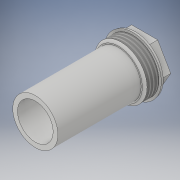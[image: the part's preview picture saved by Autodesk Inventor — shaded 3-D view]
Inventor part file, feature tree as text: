
AUTODESK INVENTOR PART (.ipt)
format: ipt  version: 2019 (Build 230136000, 136)  size: 149,504 bytes
history: native  units: mm
features: other x2, chamfer x2, sketch x2, extrude x1, projected_geometry x1
ambient origin geometry x8: Origin, YZ Plane, XZ Plane, XY Plane, X Axis, Y Axis, Z Axis, Center Point
bodies: Solide1 (feature_tree)
feature tree (8):
  other  "Révolution1"
  chamfer  "Chanfrein1"  Distance=2.0mm
  extrude  "Extrusion1"  Depth=43.0mm
  other  "Filetage1"
  chamfer  "Chanfrein2"  Distance=3.0mm
  sketch  "Esquisse1"
  sketch  "Esquisse2"
  projected_geometry  "Boucle projetée1"
